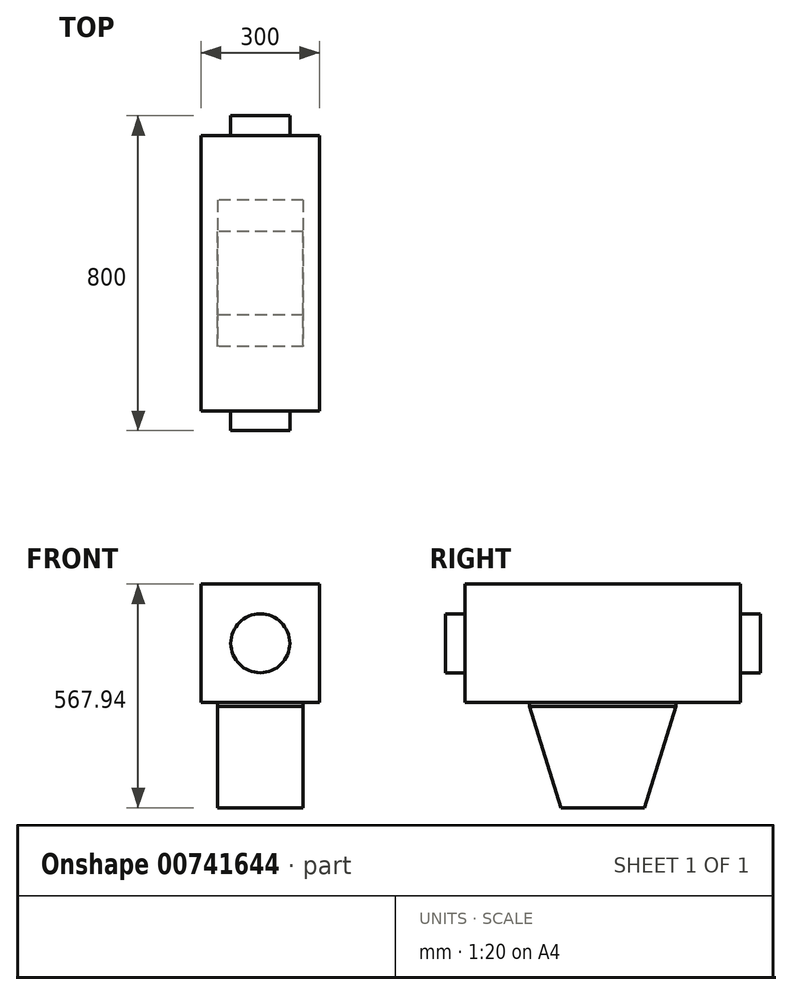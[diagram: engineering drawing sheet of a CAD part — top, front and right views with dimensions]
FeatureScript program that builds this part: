
annotation { "Feature Type Name" : "Feature", "Feature Type Description" : "" }
export const myFeature = defineFeature(function(context is Context, id is Id, definition is map)
    precondition{}
    {
        {
            var Q0;
            Q0=qCreatedBy(makeId("Right.planeOp"),FACE);
            var sketch = newSketch(context, id + "F0", { "sketchPlane" : qUnion([Q0])});
            skLineSegment(sketch, "E0.bottom", {"start": v(350, 150) * mm, "end": v(-350, 150) * mm});
            skLineSegment(sketch, "E0.top", {"start": v(350, -150) * mm, "end": v(-350, -150) * mm});
            skLineSegment(sketch, "E0.left", {"start": v(350, 150) * mm, "end": v(350, -150) * mm});
            skLineSegment(sketch, "E0.right", {"start": v(-350, 150) * mm, "end": v(-350, -150) * mm});
            skPoint(sketch, "E0.middle", {"position": v(0, 0) * mm});
            skLineSegment(sketch, "E1", {"start": v(350, 0) * mm, "end": v(350, 75) * mm});
            skSolve(sketch);
        }
        {
            var Q0;
            Q0=qSketchRegion(id+"F0",true);
            extrude(context, id + "F1", {"entities" : qUnion([Q0]), "depth" : 300 * mm});
        }
        {
            var Q0;
            Q0=makeQuery(id+"F1.opExtrude","SWEPT_FACE",FACE,{"disambiguationData":[OSD([sQuery(id+"F0.wireOp",EDGE,"E0.left"),sQuery(id+"F0.wireOp",EDGE,"E1")])]});
            var sketch = newSketch(context, id + "F2", { "sketchPlane" : qUnion([Q0])});
            skCircle(sketch, "E2", {"center": v(-150, 0) * mm, "radius": 75 * mm});
            skPoint(sketch, "E2.centerSnap0", {"position": v(-150, 150) * mm});
            skSolve(sketch);
        }
        {
            var Q0;
            Q0=qSketchRegion(id+"F2",true);
            extrude(context, id + "F3", {"entities" : qUnion([Q0]), "operationType" : NewBodyOperationType.ADD, "depth" : 50 * mm});
        }
        {
            var Q0;
            Q0=makeQuery(id+"F1.opExtrude","SWEPT_FACE",FACE,{"disambiguationData":[OSD([sQuery(id+"F0.wireOp",EDGE,"E0.top")])]});
            var sketch = newSketch(context, id + "F4", { "sketchPlane" : qUnion([Q0])});
            skLineSegment(sketch, "E3.bottom", {"start": v(41, -185.8) * mm, "end": v(259, -185.8) * mm});
            skLineSegment(sketch, "E3.top", {"start": v(41, 185.8) * mm, "end": v(259, 185.8) * mm});
            skLineSegment(sketch, "E3.left", {"start": v(41, -185.8) * mm, "end": v(41, 185.8) * mm});
            skLineSegment(sketch, "E3.right", {"start": v(259, -185.8) * mm, "end": v(259, 185.8) * mm});
            skPoint(sketch, "E3.middle", {"position": v(150, 0) * mm});
            skPoint(sketch, "E3.middle.positionSnap0", {"position": v(150, -350) * mm});
            skPoint(sketch, "E3.middle.positionSnap1", {"position": v(0, 0) * mm});
            skPoint(sketch, "E3.centerSnap0", {"position": v(150, -350) * mm});
            skPoint(sketch, "E3.centerSnap1", {"position": v(0, 0) * mm});
            skSolve(sketch);
        }
        {
            var Q0;
            Q0=qSketchRegion(id+"F4",true);
            extrude(context, id + "F5", {"entities" : qUnion([Q0]), "operationType" : NewBodyOperationType.ADD, "depth" : 10 * mm});
        }
        {
            var Q0;
            Q0=makeQuery(id+"F5.opExtrude","SWEPT_FACE",FACE,{"disambiguationData":[OSD([sQuery(id+"F4.wireOp",EDGE,"E3.left")])]});
            var sketch = newSketch(context, id + "F6", { "sketchPlane" : qUnion([Q0])});
            skLineSegment(sketch, "E4", {"start": v(-185.8, -160) * mm, "end": v(-106, -417.94) * mm});
            skLineSegment(sketch, "E5", {"start": v(185.8, -160) * mm, "end": v(106, -417.94) * mm});
            skLineSegment(sketch, "E6", {"start": v(106, -417.94) * mm, "end": v(-106, -417.94) * mm});
            skSolve(sketch);
        }
        {
            var Q0;
            Q0=makeQuery(id+"F6.imprint","IMPRINT",FACE,{"disambiguationData":[TD([[makeQuery(id+"F6.imprint","IMPRINT",EDGE,{"derivedFrom":sQuery(id+"F6.wireOp",EDGE,"E4")}),1.0]])]});
            extrude(context, id + "F7", {"entities" : qUnion([Q0]), "oppositeDirection" : true, "depth" : 218 * mm});
        }
        {
            var Q0;
            Q0=makeQuery(id+"F1.opExtrude","SWEPT_FACE",FACE,{"disambiguationData":[OSD([sQuery(id+"F0.wireOp",EDGE,"E0.right")])]});
            var sketch = newSketch(context, id + "F8", { "sketchPlane" : qUnion([Q0])});
            skPoint(sketch, "E7.centerSnap0", {"position": v(150, 150) * mm});
            skCircle(sketch, "E8", {"center": v(150, 0) * mm, "radius": 75 * mm});
            skSolve(sketch);
        }
        {
            var Q0;
            Q0=qSketchRegion(id+"F8",true);
            extrude(context, id + "F9", {"entities" : qUnion([Q0]), "operationType" : NewBodyOperationType.ADD, "depth" : 50 * mm});
        }
    });
